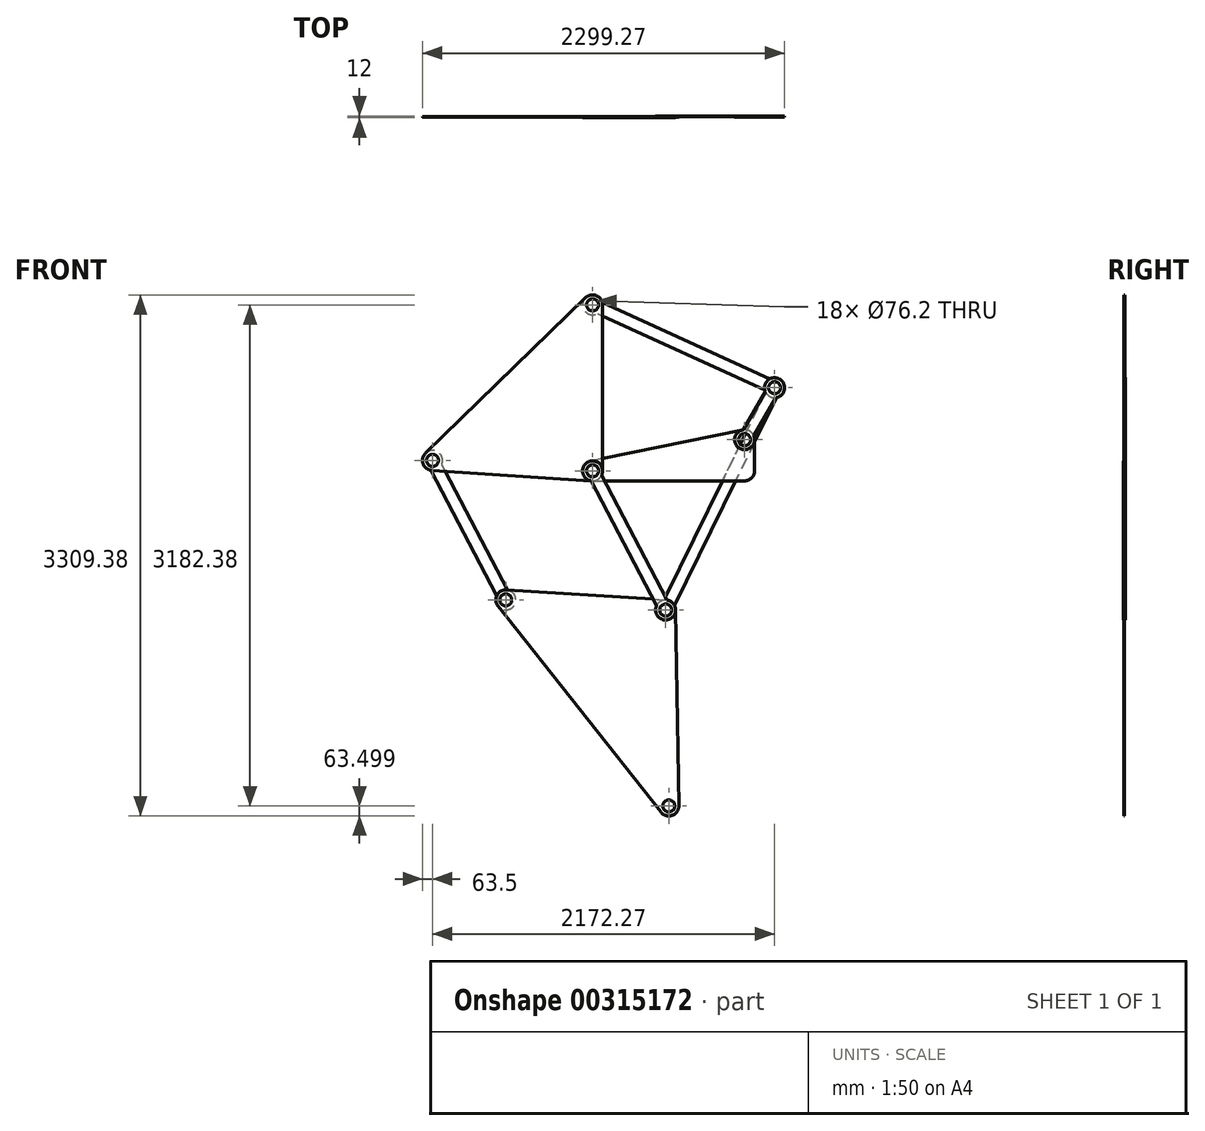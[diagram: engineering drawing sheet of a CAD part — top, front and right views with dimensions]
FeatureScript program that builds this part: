
annotation { "Feature Type Name" : "Feature", "Feature Type Description" : "" }
export const myFeature = defineFeature(function(context is Context, id is Id, definition is map)
    precondition{}
    {
        {
            assignVariable(context, id + "F0", {"name" : "Beam", "anyValue" : 3});
        }
        {
            var Q0;
            Q0=qCreatedBy(makeId("Front.planeOp"),FACE);
            cPlane(context, id + "F1", {"entities" : qUnion([Q0]), "cplaneType" : CPlaneType.OFFSET, "offset" : (getVariable(context, 'Beam')) * mm, "oppositeDirection" : true, "width" : 152.4 * mm, "height" : 152.4 * mm});
        }
        {
            var Q0;
            Q0=qCreatedBy(makeId("Front.planeOp"),FACE);
            cPlane(context, id + "F2", {"entities" : qUnion([Q0]), "cplaneType" : CPlaneType.OFFSET, "offset" : (getVariable(context, 'Beam')) * mm, "width" : 152.4 * mm, "height" : 152.4 * mm});
        }
        {
            var Q0;
            Q0=qCreatedBy(makeId("Front.planeOp"),FACE);
            var sketch = newSketch(context, id + "F3", { "sketchPlane" : qUnion([Q0])});
            skLineSegment(sketch, "E0", {"start": v(0, 0) * mm, "end": v(-1016.38, 66.3) * mm});
            skLineSegment(sketch, "E1", {"start": v(-1016.38, 66.3) * mm, "end": v(0, 1054.1) * mm});
            skLineSegment(sketch, "E2", {"start": v(0, 1054.1) * mm, "end": v(0, 0) * mm});
            skLineSegment(sketch, "E3", {"start": v(0, 1054.1) * mm, "end": v(1155.9, 527.97) * mm});
            skLineSegment(sketch, "E4", {"start": v(1155.9, 527.97) * mm, "end": v(965.2, 198.12) * mm});
            skLineSegment(sketch, "E5", {"start": v(965.2, 198.12) * mm, "end": v(965.2, 0) * mm});
            skLineSegment(sketch, "E6", {"start": v(965.2, 0) * mm, "end": v(0, 0) * mm});
            skLineSegment(sketch, "E7", {"start": v(1155.9, 527.97) * mm, "end": v(463.95, -883.85) * mm});
            skLineSegment(sketch, "E8", {"start": v(463.95, -883.85) * mm, "end": v(0, 0) * mm});
            skLineSegment(sketch, "E9", {"start": v(-1016.38, 66.3) * mm, "end": v(-551.25, -819.8) * mm});
            skLineSegment(sketch, "E10", {"start": v(-551.25, -819.8) * mm, "end": v(463.95, -883.85) * mm});
            skLineSegment(sketch, "E11", {"start": v(-551.25, -819.8) * mm, "end": v(484.48, -2128.28) * mm});
            skLineSegment(sketch, "E12", {"start": v(484.48, -2128.28) * mm, "end": v(463.95, -883.85) * mm});
            skSolve(sketch);
        }
        {
            var Q0;
            Q0=qCreatedBy(makeId("Front.planeOp"),FACE);
            var sketch = newSketch(context, id + "F4", { "sketchPlane" : qUnion([Q0])});
            skCircle(sketch, "E13", {"center": v(0, 0) * mm, "radius": 38.1 * mm});
            skCircle(sketch, "E14", {"center": v(-1016.38, 66.3) * mm, "radius": 38.1 * mm});
            skCircle(sketch, "E15", {"center": v(0, 1054.1) * mm, "radius": 38.1 * mm});
            skArc(sketch, "E16", {"start": v(-1060.64, 111.83) * mm, "mid": v(-1075.96, 44.34) * mm, "end": v(-1020.51, 2.93) * mm});
            skLineSegment(sketch, "E17", {"start": v(-1060.64, 111.83) * mm, "end": v(-44.26, 1099.64) * mm});
            skLineSegment(sketch, "E18", {"start": v(-1020.51, 2.93) * mm, "end": v(-4.13, -63.37) * mm});
            skLineSegment(sketch, "E19", {"start": v(63.5, 1054.1) * mm, "end": v(63.5, 0) * mm});
            skArc(sketch, "E20", {"start": v(63.5, 0) * mm, "mid": v(43.42, -46.34) * mm, "end": v(-4.13, -63.37) * mm});
            skArc(sketch, "E21", {"start": v(-44.26, 1099.64) * mm, "mid": v(24.72, 1112.6) * mm, "end": v(63.5, 1054.1) * mm});
            skSolve(sketch);
        }
        {
            var Q0;
            Q0=qSketchRegion(id+"F4",true);
            extrude(context, id + "F5", {"entities" : qUnion([Q0]), "depth" : (getVariable(context, 'Beam')) * mm});
        }
        {
            var Q0;
            Q0=qCreatedBy(makeId("Front.planeOp"),FACE);
            var sketch = newSketch(context, id + "F6", { "sketchPlane" : qUnion([Q0])});
            skCircle(sketch, "E22", {"center": v(-1016.38, 66.3) * mm, "radius": 38.1 * mm});
            skCircle(sketch, "E23", {"center": v(-551.25, -819.8) * mm, "radius": 38.1 * mm});
            skArc(sketch, "E24", {"start": v(-959.03, 39.02) * mm, "mid": v(-1045.9, 122.52) * mm, "end": v(-1026.5, 3.6) * mm});
            skArc(sketch, "E25", {"start": v(-608.6, -792.54) * mm, "mid": v(-521.73, -876.03) * mm, "end": v(-541.12, -757.12) * mm});
            skLineSegment(sketch, "E26", {"start": v(-1026.5, 3.6) * mm, "end": v(-608.6, -792.54) * mm});
            skLineSegment(sketch, "E27", {"start": v(-959.03, 39.02) * mm, "end": v(-541.12, -757.12) * mm});
            skLineSegment(sketch, "E28", {"start": v(-959.03, 39.02) * mm, "end": v(-1026.5, 3.6) * mm, "construction": true});
            skLineSegment(sketch, "E29", {"start": v(-541.12, -757.12) * mm, "end": v(-608.6, -792.54) * mm, "construction": true});
            skSolve(sketch);
        }
        {
            var Q0;
            Q0=qCreatedBy(id+"F1.planeOp",FACE);
            var sketch = newSketch(context, id + "F7", { "sketchPlane" : qUnion([Q0])});
            skCircle(sketch, "E30", {"center": v(0, 0) * mm, "radius": 38.1 * mm});
            skCircle(sketch, "E31", {"center": v(965.2, 198.12) * mm, "radius": 38.1 * mm});
            skLineSegment(sketch, "E32", {"start": v(0, 0) * mm, "end": v(965.2, 0) * mm, "construction": true});
            skArc(sketch, "E33", {"start": v(-12.77, 62.2) * mm, "mid": v(-63.17, -6.42) * mm, "end": v(0, -63.5) * mm});
            skLineSegment(sketch, "E34", {"start": v(0, -63.5) * mm, "end": v(965.2, -63.5) * mm});
            skLineSegment(sketch, "E35", {"start": v(965.2, 0) * mm, "end": v(965.2, 198.12) * mm, "construction": true});
            skArc(sketch, "E36", {"start": v(965.2, -63.5) * mm, "mid": v(1010.1, -44.9) * mm, "end": v(1028.7, 0) * mm});
            skLineSegment(sketch, "E37", {"start": v(1028.7, 0) * mm, "end": v(1028.7, 198.12) * mm});
            skArc(sketch, "E38", {"start": v(1028.7, 198.12) * mm, "mid": v(1005.33, 247.33) * mm, "end": v(952.43, 260.32) * mm});
            skLineSegment(sketch, "E39", {"start": v(952.43, 260.32) * mm, "end": v(-12.77, 62.2) * mm});
            skSolve(sketch);
        }
        {
            var Q0;
            Q0=qSketchRegion(id+"F7",true);
            extrude(context, id + "F8", {"entities" : qUnion([Q0]), "depth" : (getVariable(context, 'Beam')) * mm});
        }
        {
            var Q0;
            Q0=qSketchRegion(id+"F6",true);
            extrude(context, id + "F9", {"entities" : qUnion([Q0]), "oppositeDirection" : true, "depth" : (getVariable(context, 'Beam')) * mm});
        }
        {
            var Q0;
            Q0=qCreatedBy(makeId("Front.planeOp"),FACE);
            var sketch = newSketch(context, id + "F10", { "sketchPlane" : qUnion([Q0])});
            skCircle(sketch, "E40", {"center": v(0, 1054.1) * mm, "radius": 38.1 * mm});
            skCircle(sketch, "E41", {"center": v(1155.9, 527.97) * mm, "radius": 38.1 * mm});
            skArc(sketch, "E42", {"start": v(62.02, 1067.73) * mm, "mid": v(-57.8, 1080.4) * mm, "end": v(30.45, 998.38) * mm});
            skArc(sketch, "E43", {"start": v(1093.87, 514.33) * mm, "mid": v(1213.68, 501.66) * mm, "end": v(1125.44, 583.69) * mm});
            skLineSegment(sketch, "E44", {"start": v(30.45, 998.38) * mm, "end": v(1093.87, 514.33) * mm});
            skLineSegment(sketch, "E45", {"start": v(62.02, 1067.73) * mm, "end": v(1125.44, 583.69) * mm});
            skLineSegment(sketch, "E46", {"start": v(62.02, 1067.73) * mm, "end": v(30.45, 998.38) * mm, "construction": true});
            skLineSegment(sketch, "E47", {"start": v(1125.44, 583.69) * mm, "end": v(1093.87, 514.33) * mm, "construction": true});
            skSolve(sketch);
        }
        {
            var Q0;
            Q0=qSketchRegion(id+"F10",true);
            extrude(context, id + "F11", {"entities" : qUnion([Q0]), "oppositeDirection" : true, "depth" : (getVariable(context, 'Beam')) * mm});
        }
        {
            var Q0;
            Q0=qCreatedBy(makeId("Front.planeOp"),FACE);
            var sketch = newSketch(context, id + "F12", { "sketchPlane" : qUnion([Q0])});
            skCircle(sketch, "E48", {"center": v(1155.9, 527.97) * mm, "radius": 38.1 * mm});
            skCircle(sketch, "E49", {"center": v(965.2, 198.12) * mm, "radius": 38.1 * mm});
            skLineSegment(sketch, "E50", {"start": v(1023.6, 223.03) * mm, "end": v(1163.45, 464.92) * mm});
            skLineSegment(sketch, "E51", {"start": v(957.64, 261.17) * mm, "end": v(1097.48, 503.06) * mm});
            skLineSegment(sketch, "E52", {"start": v(1097.48, 503.06) * mm, "end": v(1163.45, 464.92) * mm, "construction": true});
            skLineSegment(sketch, "E53", {"start": v(957.64, 261.17) * mm, "end": v(1023.6, 223.03) * mm, "construction": true});
            skArc(sketch, "E54", {"start": v(957.64, 261.17) * mm, "mid": v(933.42, 143.15) * mm, "end": v(1023.6, 223.03) * mm});
            skArc(sketch, "E55", {"start": v(1097.48, 503.06) * mm, "mid": v(1187.67, 582.94) * mm, "end": v(1163.45, 464.92) * mm});
            skSolve(sketch);
        }
        {
            var Q0;
            Q0=qCreatedBy(makeId("Front.planeOp"),FACE);
            var sketch = newSketch(context, id + "F13", { "sketchPlane" : qUnion([Q0])});
            skCircle(sketch, "E56", {"center": v(463.95, -883.85) * mm, "radius": 38.1 * mm});
            skCircle(sketch, "E57", {"center": v(484.48, -2128.28) * mm, "radius": 38.1 * mm});
            skCircle(sketch, "E58", {"center": v(-551.25, -819.8) * mm, "radius": 38.1 * mm});
            skArc(sketch, "E59", {"start": v(434.69, -2167.7) * mm, "mid": v(505.84, -2188.08) * mm, "end": v(547.97, -2127.23) * mm});
            skLineSegment(sketch, "E60", {"start": v(434.69, -2167.7) * mm, "end": v(-601.04, -859.22) * mm});
            skLineSegment(sketch, "E61", {"start": v(547.97, -2127.23) * mm, "end": v(527.44, -882.8) * mm});
            skLineSegment(sketch, "E62", {"start": v(-547.25, -756.43) * mm, "end": v(467.95, -820.48) * mm});
            skArc(sketch, "E63", {"start": v(467.95, -820.48) * mm, "mid": v(509.89, -840) * mm, "end": v(527.44, -882.8) * mm});
            skArc(sketch, "E64", {"start": v(-601.04, -859.22) * mm, "mid": v(-607.5, -790.37) * mm, "end": v(-547.25, -756.43) * mm});
            skSolve(sketch);
        }
        {
            var Q0;
            Q0=qCreatedBy(id+"F2.planeOp",FACE);
            var sketch = newSketch(context, id + "F14", { "sketchPlane" : qUnion([Q0])});
            skCircle(sketch, "E65", {"center": v(0, 0) * mm, "radius": 38.1 * mm});
            skCircle(sketch, "E66", {"center": v(463.95, -883.85) * mm, "radius": 38.1 * mm});
            skArc(sketch, "E67", {"start": v(57.35, -27.27) * mm, "mid": v(-29.51, 56.22) * mm, "end": v(-10.12, -62.69) * mm});
            skArc(sketch, "E68", {"start": v(406.6, -856.58) * mm, "mid": v(493.47, -940.07) * mm, "end": v(474.08, -821.16) * mm});
            skLineSegment(sketch, "E69", {"start": v(-10.12, -62.69) * mm, "end": v(406.6, -856.58) * mm});
            skLineSegment(sketch, "E70", {"start": v(57.35, -27.27) * mm, "end": v(474.08, -821.16) * mm});
            skLineSegment(sketch, "E71", {"start": v(57.35, -27.27) * mm, "end": v(-10.12, -62.69) * mm, "construction": true});
            skLineSegment(sketch, "E72", {"start": v(474.08, -821.16) * mm, "end": v(406.6, -856.58) * mm, "construction": true});
            skSolve(sketch);
        }
        {
            var Q0;
            Q0=qCreatedBy(id+"F1.planeOp",FACE);
            var sketch = newSketch(context, id + "F15", { "sketchPlane" : qUnion([Q0])});
            skCircle(sketch, "E73", {"center": v(1155.9, 527.97) * mm, "radius": 38.1 * mm});
            skCircle(sketch, "E74", {"center": v(463.95, -883.85) * mm, "radius": 38.1 * mm});
            skArc(sketch, "E75", {"start": v(1167.75, 465.58) * mm, "mid": v(1183.84, 584.99) * mm, "end": v(1099.32, 499.12) * mm});
            skArc(sketch, "E76", {"start": v(452.1, -821.47) * mm, "mid": v(436, -940.87) * mm, "end": v(520.52, -855) * mm});
            skLineSegment(sketch, "E77", {"start": v(1099.32, 499.12) * mm, "end": v(452.1, -821.47) * mm});
            skLineSegment(sketch, "E78", {"start": v(1167.75, 465.58) * mm, "end": v(520.52, -855) * mm});
            skLineSegment(sketch, "E79", {"start": v(1167.75, 465.58) * mm, "end": v(1099.32, 499.12) * mm, "construction": true});
            skLineSegment(sketch, "E80", {"start": v(520.52, -855) * mm, "end": v(452.1, -821.47) * mm, "construction": true});
            skSolve(sketch);
        }
        {
            var Q0;
            Q0=qSketchRegion(id+"F13",true);
            extrude(context, id + "F16", {"entities" : qUnion([Q0]), "depth" : (getVariable(context, 'Beam')) * mm});
        }
        {
            var Q0;
            Q0=qSketchRegion(id+"F15",true);
            extrude(context, id + "F17", {"entities" : qUnion([Q0]), "oppositeDirection" : true, "depth" : (getVariable(context, 'Beam')) * mm});
        }
        {
            var Q0;
            Q0=qSketchRegion(id+"F14",true);
            extrude(context, id + "F18", {"entities" : qUnion([Q0]), "depth" : (getVariable(context, 'Beam')) * mm});
        }
        {
            var Q0;
            Q0=qSketchRegion(id+"F12",true);
            extrude(context, id + "F19", {"entities" : qUnion([Q0]), "depth" : (getVariable(context, 'Beam')) * mm});
        }
    });
